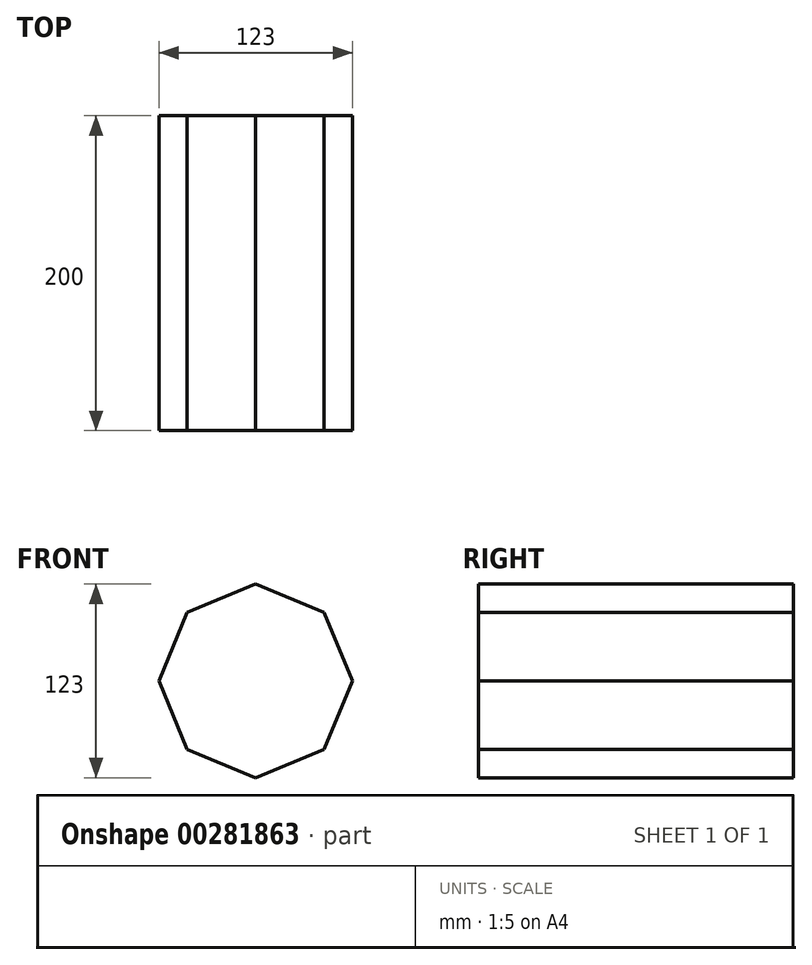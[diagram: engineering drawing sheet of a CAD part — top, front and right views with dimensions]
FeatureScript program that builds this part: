
annotation { "Feature Type Name" : "Feature", "Feature Type Description" : "" }
export const myFeature = defineFeature(function(context is Context, id is Id, definition is map)
    precondition{}
    {
        {
            var Q0;
            Q0=qCreatedBy(makeId("Front.planeOp"),FACE);
            var sketch = newSketch(context, id + "F0", { "sketchPlane" : qUnion([Q0])});
            skCircle(sketch, "E0.cCircle", {"center": v(-2.62, 0) * mm, "radius": 61.5 * mm, "construction": true});
            skLineSegment(sketch, "E0.0", {"start": v(58.88, 0) * mm, "end": v(40.86, -43.49) * mm});
            skLineSegment(sketch, "E0.1", {"start": v(40.86, -43.49) * mm, "end": v(-2.62, -61.5) * mm});
            skLineSegment(sketch, "E0.2", {"start": v(-2.62, -61.5) * mm, "end": v(-46.11, -43.49) * mm});
            skLineSegment(sketch, "E0.3", {"start": v(-46.11, -43.49) * mm, "end": v(-64.12, 0) * mm});
            skLineSegment(sketch, "E0.4", {"start": v(-64.12, 0) * mm, "end": v(-46.11, 43.49) * mm});
            skLineSegment(sketch, "E0.5", {"start": v(-46.11, 43.49) * mm, "end": v(-2.62, 61.5) * mm});
            skLineSegment(sketch, "E0.6", {"start": v(-2.62, 61.5) * mm, "end": v(40.86, 43.49) * mm});
            skLineSegment(sketch, "E0.7", {"start": v(40.86, 43.49) * mm, "end": v(58.88, 0) * mm});
            skSolve(sketch);
        }
        {
            var Q0;
            Q0=makeQuery(id+"F0.imprint","IMPRINT",FACE,{"disambiguationData":[TD([[makeQuery(id+"F0.imprint","IMPRINT",EDGE,{"derivedFrom":sQuery(id+"F0.wireOp",EDGE,"E0.0")}),-1.0]])]});
            extrude(context, id + "F1", {"entities" : qUnion([Q0]), "depth" : 200 * mm});
        }
    });
